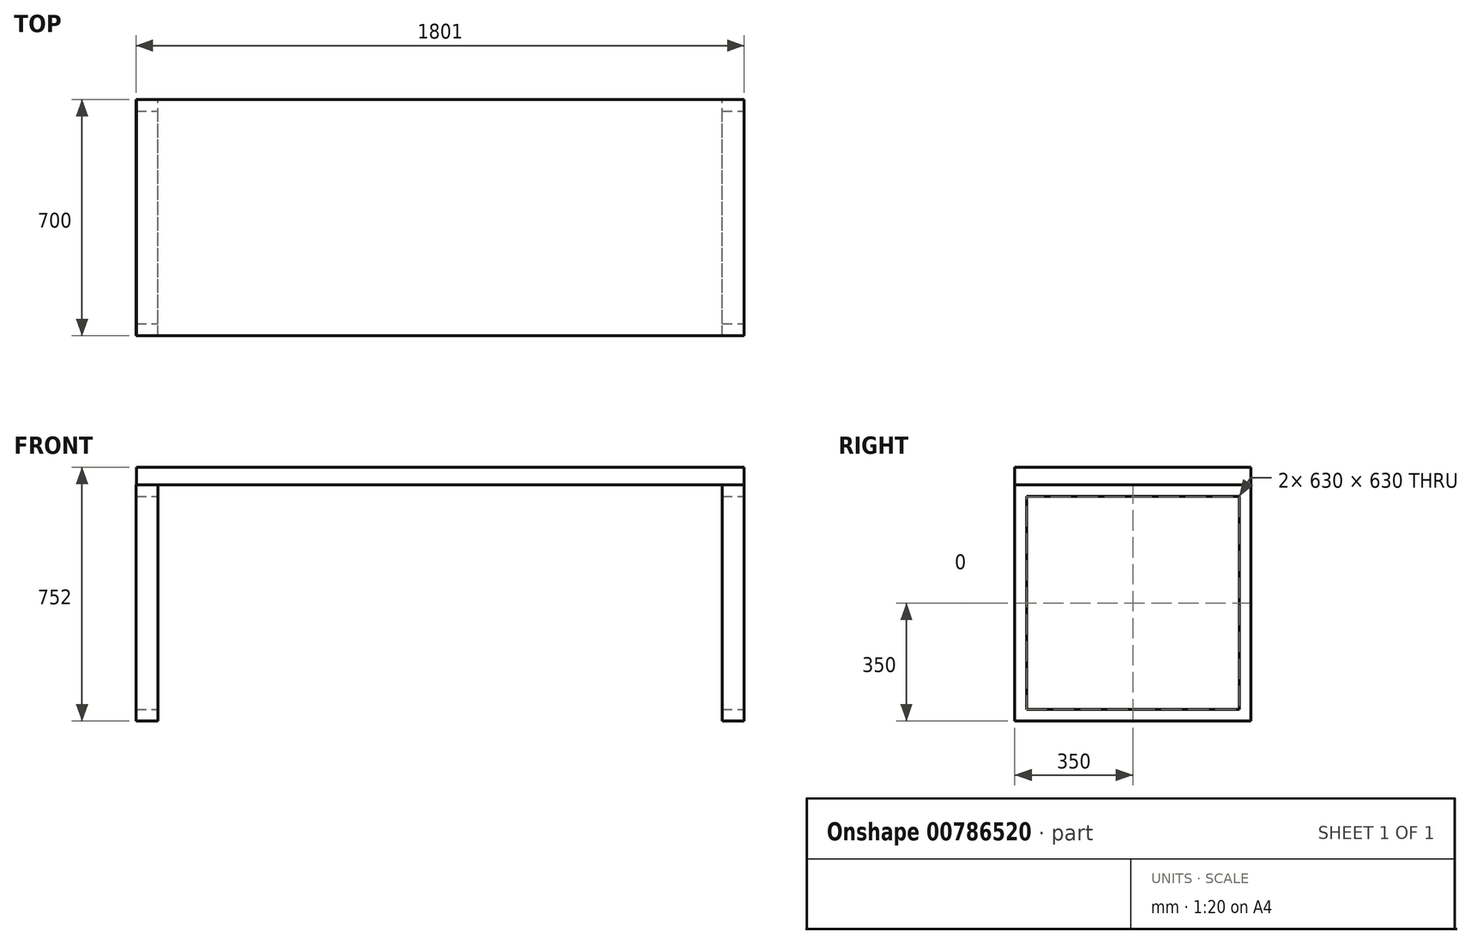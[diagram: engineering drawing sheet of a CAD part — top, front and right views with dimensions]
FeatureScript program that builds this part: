
annotation { "Feature Type Name" : "Feature", "Feature Type Description" : "" }
export const myFeature = defineFeature(function(context is Context, id is Id, definition is map)
    precondition{}
    {
        {
            var Q0;
            Q0=qCreatedBy(makeId("Top.planeOp"),FACE);
            var sketch = newSketch(context, id + "F0", { "sketchPlane" : qUnion([Q0])});
            skLineSegment(sketch, "E0.bottom", {"start": v(0, 0) * mm, "end": v(1800, 0) * mm});
            skLineSegment(sketch, "E0.top", {"start": v(0, 700) * mm, "end": v(1800, 700) * mm});
            skLineSegment(sketch, "E0.left", {"start": v(0, 0) * mm, "end": v(0, 700) * mm});
            skLineSegment(sketch, "E0.right", {"start": v(1800, 0) * mm, "end": v(1800, 700) * mm});
            skSolve(sketch);
        }
        {
            var Q0;
            Q0=makeQuery(id+"F0.imprint","IMPRINT",FACE,{"disambiguationData":[TD([[makeQuery(id+"F0.imprint","IMPRINT",EDGE,{"derivedFrom":sQuery(id+"F0.wireOp",EDGE,"E0.bottom")}),1.0]])]});
            extrude(context, id + "F1", {"entities" : qUnion([Q0]), "depth" : 52 * mm, "offsetDistance" : 25 * mm});
        }
        {
            var Q0;
            Q0=makeQuery(id+"F1.opExtrude","SWEPT_FACE",FACE,{"disambiguationData":[OSD([sQuery(id+"F0.wireOp",EDGE,"E0.right")])]});
            var sketch = newSketch(context, id + "F2", { "sketchPlane" : qUnion([Q0])});
            skLineSegment(sketch, "E1.bottom", {"start": v(0, 0) * mm, "end": v(700, 0) * mm});
            skLineSegment(sketch, "E1.top", {"start": v(0, -700) * mm, "end": v(700, -700) * mm});
            skLineSegment(sketch, "E1.left", {"start": v(0, 0) * mm, "end": v(0, -700) * mm});
            skLineSegment(sketch, "E1.right", {"start": v(700, 0) * mm, "end": v(700, -700) * mm});
            skLineSegment(sketch, "E2.bottom", {"start": v(35, -35) * mm, "end": v(665, -35) * mm});
            skLineSegment(sketch, "E2.top", {"start": v(35, -665) * mm, "end": v(665, -665) * mm});
            skLineSegment(sketch, "E2.left", {"start": v(35, -35) * mm, "end": v(35, -665) * mm});
            skLineSegment(sketch, "E2.right", {"start": v(665, -35) * mm, "end": v(665, -665) * mm});
            skSolve(sketch);
        }
        {
            var Q0;
            Q0=makeQuery(id+"F2.imprint","IMPRINT",FACE,{"disambiguationData":[TD([[makeQuery(id+"F2.imprint","IMPRINT",EDGE,{"derivedFrom":sQuery(id+"F2.wireOp",EDGE,"E1.bottom")}),-1.0]])]});
            extrude(context, id + "F3", {"entities" : qUnion([Q0]), "oppositeDirection" : true, "depth" : 65 * mm, "offsetDistance" : 25 * mm});
        }
        {
            var Q0;
            Q0=makeQuery(id+"F3.opExtrude","SWEPT_BODY",BODY,{"disambiguationData":[OSD([sQuery(id+"F2.wireOp",EDGE,"E1.bottom"),sQuery(id+"F2.wireOp",EDGE,"E1.top"),sQuery(id+"F2.wireOp",EDGE,"E1.left"),sQuery(id+"F2.wireOp",EDGE,"E1.right"),sQuery(id+"F2.wireOp",EDGE,"E2.bottom"),sQuery(id+"F2.wireOp",EDGE,"E2.top"),sQuery(id+"F2.wireOp",EDGE,"E2.left"),sQuery(id+"F2.wireOp",EDGE,"E2.right")])]});
            transform(context, id + "F4", {"entities" : qUnion([Q0]), "transformType" : TransformType.TRANSLATION_3D, "dx" : -1736 * mm, "dy" : 0 * mm, "dz" : 0 * mm, "makeCopy" : true});
        }
    });
